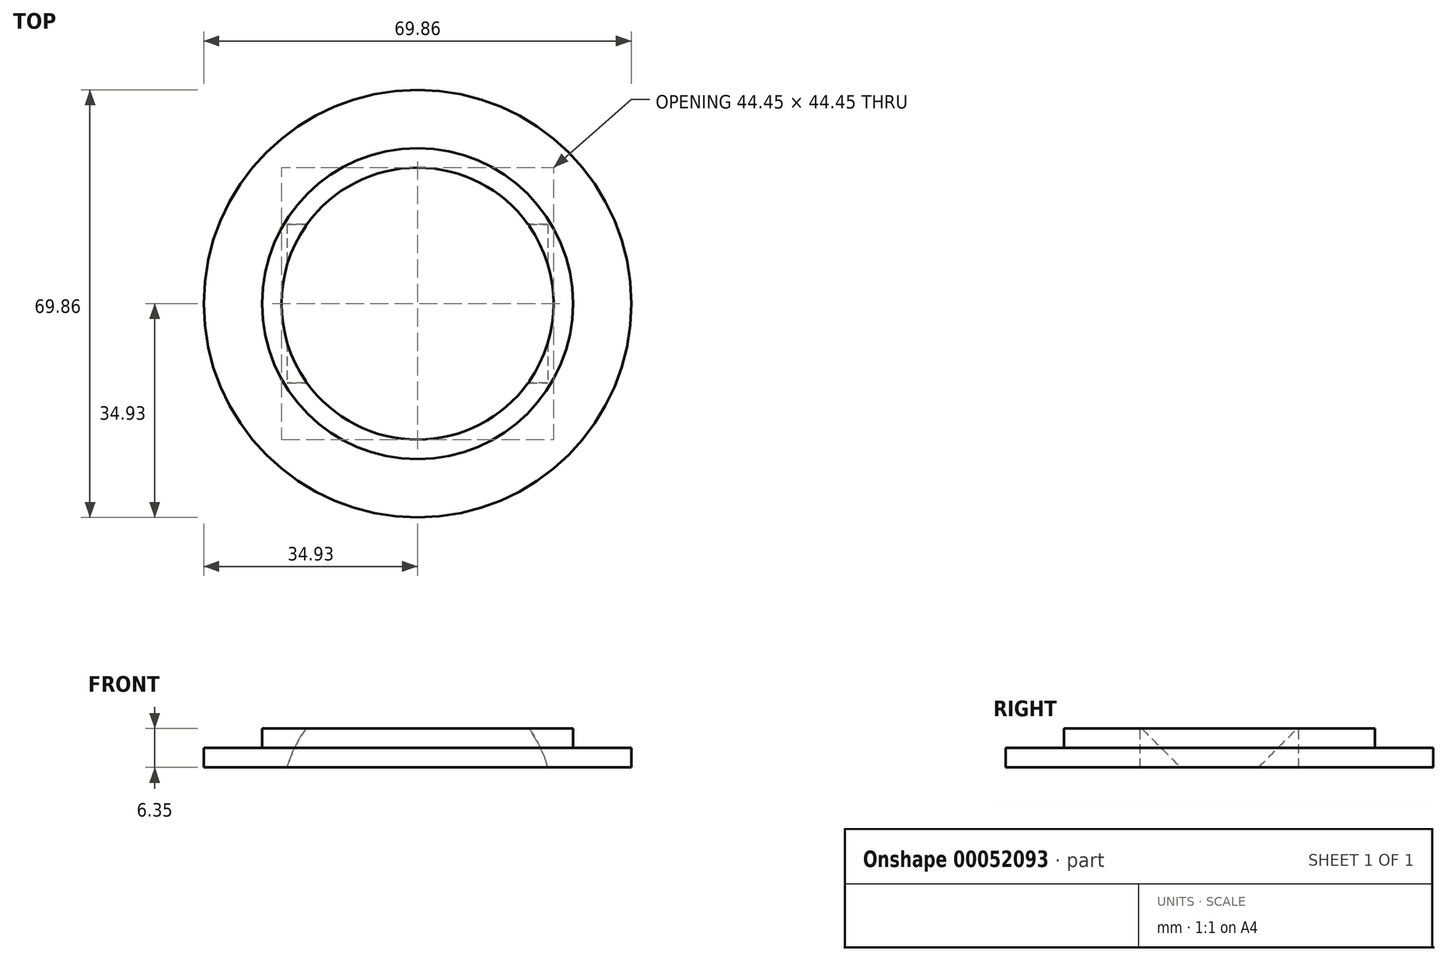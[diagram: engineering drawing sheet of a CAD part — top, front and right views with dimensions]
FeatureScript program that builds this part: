
annotation { "Feature Type Name" : "Feature", "Feature Type Description" : "" }
export const myFeature = defineFeature(function(context is Context, id is Id, definition is map)
    precondition{}
    {
        {
            var Q0;
            Q0=qCreatedBy(makeId("Top.planeOp"),FACE);
            var sketch = newSketch(context, id + "F0", { "sketchPlane" : qUnion([Q0])});
            skCircle(sketch, "E0", {"center": v(0, 0) * mm, "radius": 22.23 * mm});
            skCircle(sketch, "E1.0", {"center": v(0, 0) * mm, "radius": 34.93 * mm});
            skCircle(sketch, "E2.0", {"center": v(0, 0) * mm, "radius": 25.4 * mm});
            skSolve(sketch);
        }
        {
            var Q0;
            Q0 = qSketchRegion(id + "F0", true);
            extrude(context, id + "F1", {"entities" : qUnion([Q0]), "depth" : 3.17 * mm});
        }
        {
            var Q0;
            Q0=makeQuery(id+"F0.imprint","IMPRINT",FACE,{"disambiguationData":[TD([[makeQuery(id+"F0.imprint","IMPRINT",EDGE,{"derivedFrom":sQuery(id+"F0.wireOp",EDGE,"E0")}),-1.0]])]});
            extrude(context, id + "F2", {"entities" : qUnion([Q0]), "operationType" : NewBodyOperationType.ADD, "depth" : 6.35 * mm});
        }
        {
            var Q0;
            Q0=qCreatedBy(makeId("Front.planeOp"),FACE);
            var sketch = newSketch(context, id + "F3", { "sketchPlane" : qUnion([Q0])});
            skCircle(sketch, "E3", {"center": v(0, -6.35) * mm, "radius": 22.23 * mm});
            skSolve(sketch);
        }
        {
            var Q0;
            Q0=makeQuery(id+"F3.imprint","IMPRINT",FACE,{"disambiguationData":[TD([[makeQuery(id+"F3.imprint","IMPRINT",EDGE,{"derivedFrom":sQuery(id+"F3.wireOp",EDGE,"E3")}),1.0]])]});
            extrude(context, id + "F4", {"entities" : qUnion([Q0]), "operationType" : NewBodyOperationType.REMOVE, "oppositeDirection" : true, "depth" : 12.95 * mm, "hasSecondDirection" : true, "secondDirectionOppositeDirection" : false, "secondDirectionDepth" : 12.95 * mm});
        }
    });
